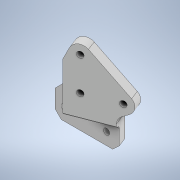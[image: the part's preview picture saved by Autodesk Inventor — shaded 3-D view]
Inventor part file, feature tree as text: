
AUTODESK INVENTOR PART (.ipt)
format: ipt  version: 2020 (Build 240168000, 168)  size: 294,912 bytes
history: native  units: mm
features: reference x11, extrude x9, sketch x9, projected_geometry x8, other x7, fillet x6, chamfer x4, thicken_offset x2
ambient origin geometry x8: Origin, YZ Plane, XZ Plane, XY Plane, X Axis, Y Axis, Z Axis, Center Point
bodies: Solid1 (feature_tree)
feature tree (56):
  extrude  "Extrusion1"  Depth=20.0mm
  extrude  "Extrusion2"  Depth=2.0mm
  extrude  "Extrusion3"  Depth=3.0mm TaperAngle=0.0deg
  extrude  "Extrusion4"  Depth=3.0mm TaperAngle=0.0deg
  extrude  "Extrusion5"  Depth=6.0mm
  extrude  "Extrusion6"  Depth=3.0mm
  extrude  "Extrusion7"  Depth=3.0mm TaperAngle=0.0deg
  fillet  "Fillet1"  Radius=6.0mm
  fillet  "Fillet2"  Radius=120.0mm
  chamfer  "Chamfer1"  Distance=3.0mm Angle=45.0deg
  extrude  "Extrusion8"  Depth=2.0mm
  extrude  "Extrusion9"  Depth=2.0mm
  chamfer  "Chamfer3"  Distance=2.0mm
  chamfer  "Chamfer4"  Distance=120.0mm
  thicken_offset  "Thicken1"
  thicken_offset  "Thicken2"
  fillet  "Fillet6"  Radius=120.0mm
  fillet  "Fillet7"  Radius=2.0mm
  fillet  "Fillet8"  Radius=2.0mm
  chamfer  "Chamfer5"  Distance=2.0mm
  fillet  "Fillet10"  Radius=1.5mm
  sketch  "Sketch1"  dims[d0=8.0mm d1=20.0mm]
  reference  "Reference1"
  reference  "Reference2"
  reference  "Reference3"
  sketch  "Sketch2"  dims[d2=2.0mm d3=2.0mm]
  projected_geometry  "Projected Loop1"
  reference  "Reference4"
  sketch  "Sketch3"  dims[d4=3.0mm d5=0.0mm d6=20.0mm d7=0.0mm]
  projected_geometry  "Projected Loop2"
  projected_geometry  "Projected Loop3"
  sketch  "Sketch4"  dims[d8=3.0mm d9=0.0mm d10=3.0mm d11=0.0mm]
  projected_geometry  "Projected Loop4"
  sketch  "Sketch5"  dims[d12=6.0mm d13=6.0mm]
  reference  "Reference5"
  reference  "Reference6"
  projected_geometry  "Projected Loop5"
  sketch  "Sketch6"  dims[d14=3.0mm d15=0.0mm d16=6.0mm]
  reference  "Reference7"
  reference  "Reference8"
  projected_geometry  "Projected Loop6"
  sketch  "Sketch7"  dims[d17=6.0mm d18=3.0mm d19=0.0mm d20=6.0mm d21=120.0mm d22=0.0mm]
  projected_geometry  "Projected Loop7"
  sketch  "Sketch8"  dims[d23=3.0mm]
  reference  "Reference9"
  reference  "Reference10"
  reference  "Reference11"
  sketch  "Sketch9"  dims[d24=1.0mm d25=3.0mm d26=2.0mm d27=45.0deg d28=2.0mm d29=2.0mm d30=2.0mm d31=120.0mm d32=0.0mm d33=120.0mm d34=0.0mm d41=2.0mm d42=2.0mm d43=45.0deg d44=2.0mm d45=2.0mm d46=45.0deg d47=2.0mm d48=1.0mm d49=1.5mm d50=1.5mm d51=2.0mm d52=3.0mm d53=1.5mm d54=0.5mm d55=2.0mm d56=45.0deg d58=2.0mm]
  projected_geometry  "Projected Loop8"
  parser-record x1  (decoder bookkeeping rows leaked as tree rows — omitted from the tree; the rows remain in map.json)
  other  "leg_1.iam"
  other  "leg_holder_2:1"
  other  "wh_ass_3:3"
  other  "screw_holder_2_3:2"
  other  "screw_holder_2_3:5"
  other  "tendon_wh_3:1"
note: 1 file-system path scrubbed to <path> (originals preserved in map.json)
